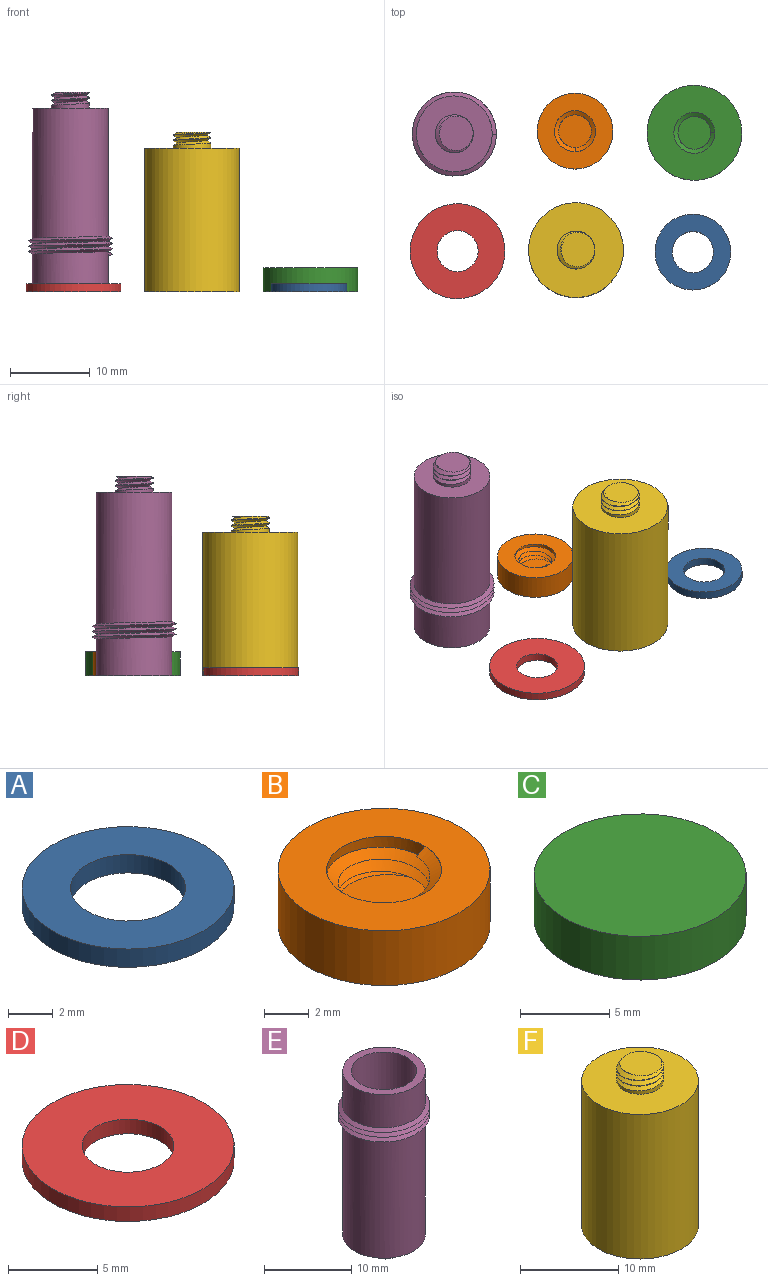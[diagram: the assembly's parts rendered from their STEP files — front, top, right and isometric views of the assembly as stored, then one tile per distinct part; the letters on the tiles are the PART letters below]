
ASSEMBLY  parts=6 mates=5
PART A: 4 faces, bbox 9.5x9.5x1 mm
  f0: cylinder r=2.58mm len=5.15mm, axis (0,0,1), area 16.2mm2, adj f2,f3
  f1: cylinder r=4.75mm len=9.5mm, axis (0,0,1), area 29.8mm2, adj f2,f3
  f2: plane 9.5x9.5mm, normal (0,0,-1), area 50.1mm2, adj f0,f1
  f3: plane 9.5x9.5mm, normal (0,0,1), area 50.1mm2, adj f0,f1
PART B: 8 faces, bbox 9.9x9.9x3.4 mm
  f0: cylinder r=2.58mm len=5.15mm, axis (0,0,1), area 7.6mm2, adj f2,f3,f5,f6,f7
  f1: cylinder r=4.75mm len=9.5mm, axis (0,0,1), area 89.5mm2, adj f2,f4
  f2: plane 9.5x9.5mm, normal (0,0,1), area 50.1mm2, adj f0,f1
  f3: plane 5.1x5.09mm, normal (0,0,1), area 17.3mm2, adj f0,f5,f6
  f4: plane 9.5x9.5mm, normal (0,0,-1), area 70.9mm2, adj f1
  f5: bspline ~5.95x5.15mm, area 24.3mm2, adj f0,f3,f6,f7
  f6: bspline ~5.95x5.15mm, area 20.2mm2, adj f0,f3,f5,f7
  f7: plane 0.6x0.52mm, normal (0,1,0), area 0.2mm2, adj f0,f5,f6
PART C: 8 faces, bbox 12.3x12.3x3.4 mm
  f0: cylinder r=2.58mm len=5.15mm, axis (0,0,-1), area 7.6mm2, adj f2,f3,f5,f6,f7
  f1: cylinder r=5.95mm len=11.9mm, axis (0,0,-1), area 112.2mm2, adj f2,f4
  f2: plane 11.9x11.9mm, normal (0,0,-1), area 90.4mm2, adj f0,f1
  f3: plane 5.1x5.09mm, normal (0,0,-1), area 17.3mm2, adj f0,f5,f6
  f4: plane 11.9x11.9mm, normal (0,0,1), area 111.2mm2, adj f1
  f5: bspline ~5.95x5.15mm, area 24.3mm2, adj f0,f3,f6,f7
  f6: bspline ~5.95x5.15mm, area 20.2mm2, adj f0,f3,f5,f7
  f7: plane 0.6x0.52mm, normal (0,-1,0), area 0.2mm2, adj f0,f5,f6
PART D: 4 faces, bbox 11.9x11.9x1 mm
  f0: cylinder r=2.58mm len=5.15mm, axis (0,0,-1), area 16.2mm2, adj f2,f3
  f1: cylinder r=5.95mm len=11.9mm, axis (0,0,-1), area 37.4mm2, adj f2,f3
  f2: plane 11.9x11.9mm, normal (0,0,1), area 90.4mm2, adj f0,f1
  f3: plane 11.9x11.9mm, normal (0,0,-1), area 90.4mm2, adj f0,f1
PART E: 17 faces, bbox 10.9x12.6x25.8 mm
  f0: cylinder r=2.38mm len=4.75mm, axis (0,0,1), area 7mm2, adj f12,f13,f14,f15,f16
  f1: cylinder r=3.75mm len=22mm, axis (0,0,-1), area 518.4mm2, adj f6,f7
  f2: cylinder r=4.75mm len=9.5mm, axis (0,0,-1), area 141.3mm2, adj f4,f6,f8,f11
  f3: cylinder r=4.75mm len=9.5mm, axis (0,0,-1), area 2mm2, adj f4,f5,f10,f11
  f4: cylinder r=4.75mm len=9.5mm, axis (0,0,-1), area 2mm2, adj f2,f3,f10,f11
  f5: cylinder r=4.75mm len=16.67mm, axis (0,0,-1), area 487.5mm2, adj f3,f9,f10,f12
  f6: plane 9.5x9.5mm, normal (0,0,1), area 26.7mm2, adj f1,f2
  f7: plane 7.5x7.5mm, normal (0,0,1), area 44.2mm2, adj f1
  f8: plane 0.6x0.52mm, normal (0,1,0), area 0.2mm2, adj f2,f10,f11
  f9: plane 0.6x0.52mm, normal (0,-1,0), area 0.2mm2, adj f5,f10,f11
  f10: bspline ~12.17x10.54mm, area 56.7mm2, adj f3,f4,f5,f8,f9,f11
  f11: bspline ~12.17x10.54mm, area 56.7mm2, adj f2,f3,f4,f8,f9,f10
  f12: plane 9.5x9.5mm, normal (0,0,-1), area 53.2mm2, adj f0,f5
  f13: plane 4.7x4.69mm, normal (0,0,-1), area 14.5mm2, adj f0,f15,f16
  f14: plane 0.6x0.52mm, normal (0,-1,0), area 0.2mm2, adj f0,f15,f16
  f15: bspline ~5.49x4.75mm, area 22.2mm2, adj f0,f13,f14,f16
  f16: bspline ~5.49x4.75mm, area 18.5mm2, adj f0,f13,f14,f15
PART F: 16 faces, bbox 12.3x13.1x21.2 mm
  f0: cylinder r=2.38mm len=4.75mm, axis (0,0,-1), area 7mm2, adj f2,f12,f13,f14,f15
  f1: cylinder r=5.95mm len=18mm, axis (0,0,-1), area 672.9mm2, adj f2,f3
  f2: plane 11.9x11.9mm, normal (0,0,1), area 93.5mm2, adj f0,f1
  f3: plane 12.33x12.33mm, normal (0,0,-1), area 26.7mm2, adj f1,f4,f5,f11
  f4: bspline ~12.63x10.94mm, area 54.4mm2, adj f3,f5,f6,f8,f9,f10
  f5: bspline ~12.63x10.94mm, area 45.8mm2, adj f3,f4,f6,f9,f10,f11
  f6: plane 0.6x0.52mm, normal (0,-1,0), area 0.2mm2, adj f4,f5,f8
  f7: plane 9.9x9.9mm, normal (0,0,-1), area 77mm2, adj f8
  f8: cylinder r=4.95mm len=15.67mm, axis (0,0,-1), area 476.9mm2, adj f4,f6,f7,f9
  f9: cylinder r=4.95mm len=9.9mm, axis (0,0,-1), area 2.1mm2, adj f4,f5,f8,f10
  f10: cylinder r=4.95mm len=9.9mm, axis (0,0,-1), area 2.1mm2, adj f4,f5,f9,f11
  f11: cylinder r=4.95mm len=2.89mm, axis (0,0,-1), area 0.1mm2, adj f3,f5,f10
  f12: plane 4.7x4.69mm, normal (0,0,1), area 14.5mm2, adj f0,f14,f15
  f13: plane 0.6x0.52mm, normal (0,1,0), area 0.2mm2, adj f0,f14,f15
  f14: bspline ~5.49x4.75mm, area 22.2mm2, adj f0,f12,f13,f15
  f15: bspline ~5.49x4.75mm, area 18.5mm2, adj f0,f12,f13,f14
PLACE A rot(axis=(0.71,-0.71,0),180deg) t=(14.81,-8.75,-52.22)mm
PLACE B rot(axis=(0,0,-1),90deg) t=(0.03,6.42,-46.22)mm
PLACE C rot(axis=(1,0,0),180deg) t=(14.99,6.21,-14.22)mm
PLACE D rot(axis=(1,0,0),180deg) t=(-14.71,-8.63,-17.22)mm
PLACE E rot(axis=(1,0,0),180deg) t=(-15.11,6.05,-29.22)mm
PLACE F t=(0.14,-8.53,-66.22)mm
MATE planar C.f1 <-> D.f1  axis (0,0,-1) through (14.99,6.21,-51.22)mm
MATE planar B.f1 <-> F.f1  axis (0,0,-1) through (0.03,6.42,-51.22)mm
MATE planar E.f2 <-> F.f8  axis (0,0,-1) through (-15.11,6.05,-51.22)mm
MATE planar D.f1 <-> A.f0  axis (0,0,-1) through (-14.71,-8.63,-51.22)mm
MATE planar F.f1 <-> A.f0  axis (0,0,-1) through (0.14,-8.53,-51.22)mm
